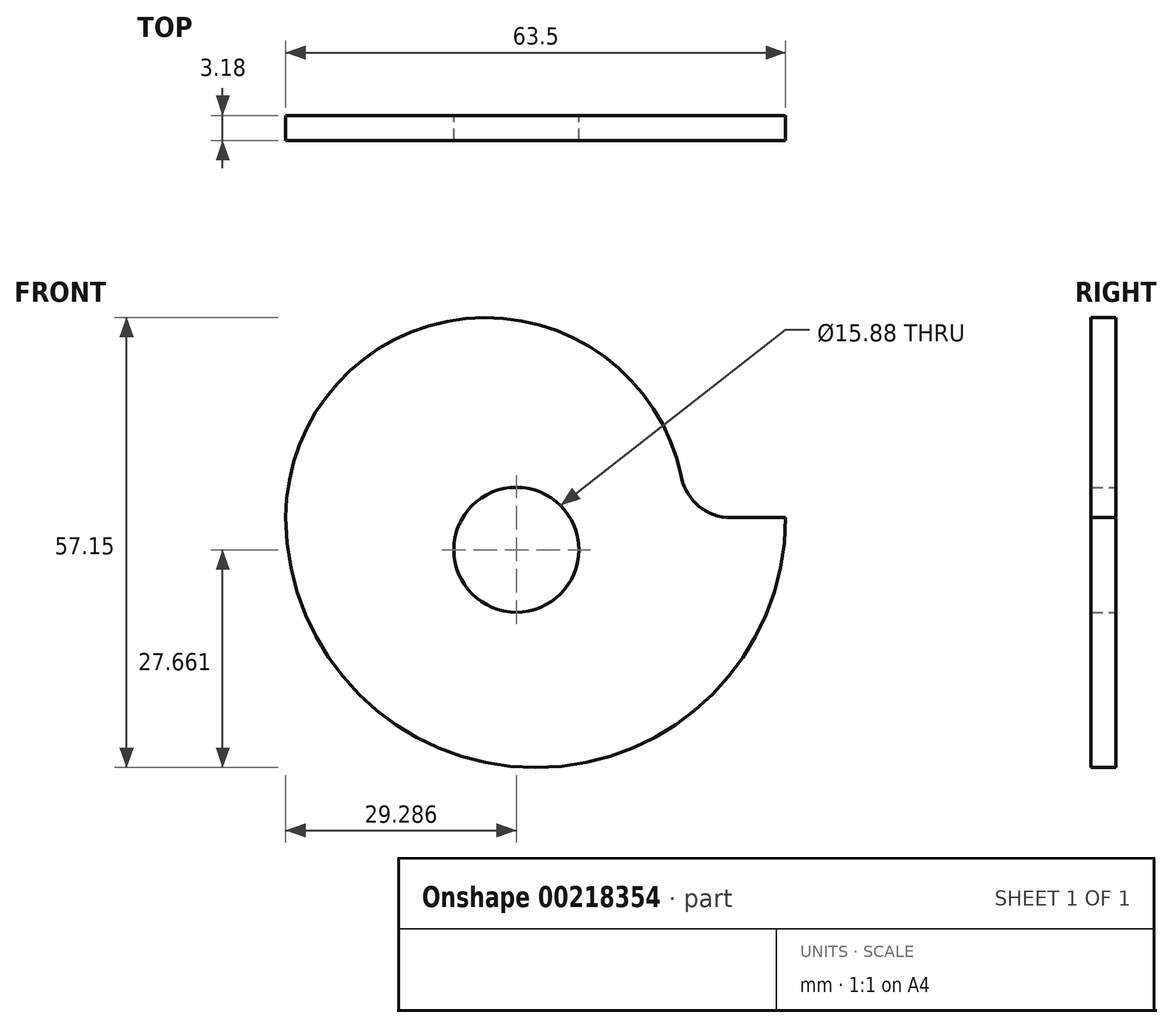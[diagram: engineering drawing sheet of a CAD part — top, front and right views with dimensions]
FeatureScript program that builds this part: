
annotation { "Feature Type Name" : "Feature", "Feature Type Description" : "" }
export const myFeature = defineFeature(function(context is Context, id is Id, definition is map)
    precondition{}
    {
        {
            var Q0;
            Q0=qCreatedBy(makeId("Front.planeOp"),FACE);
            var sketch = newSketch(context, id + "F0", { "sketchPlane" : qUnion([Q0])});
            skArc(sketch, "E0", {"start": v(-31.75, 0) * mm, "mid": v(0, -31.75) * mm, "end": v(31.75, 0) * mm});
            skArc(sketch, "E1", {"start": v(18.54, 5.08) * mm, "mid": v(-8.9, 25.27) * mm, "end": v(-31.75, 0) * mm});
            skLineSegment(sketch, "E2", {"start": v(24.76, 0) * mm, "end": v(31.75, 0) * mm});
            skCircle(sketch, "E3", {"center": v(-2.46, -4.09) * mm, "radius": 7.94 * mm});
            skPoint(sketch, "E4.visualSharp", {"position": v(19.05, 0) * mm});
            skArc(sketch, "E4.filletArc", {"start": v(18.54, 5.08) * mm, "mid": v(20.74, 1.43) * mm, "end": v(24.76, 0) * mm});
            skSolve(sketch);
        }
        {
            var Q0;
            Q0 = qSketchRegion(id + "F0", true);
            extrude(context, id + "F1", {"entities" : qUnion([Q0]), "depth" : 3.17 * mm});
        }
    });
